# Revit family: Haworth_Epure_Pedestal_Mobile_EU_PRELIMINARY
name_source: partatom
category: Furniture
units: mm (PartAtom-declared; Revit-internal decimal feet)

## family parameters
Always vertical = Yes
Cut with Voids When Loaded = No
OmniClass Number = 23.40.70.14.64.11
OmniClass Title = Office Furniture
Room Calculation Point = No
Shared = No
Work Plane-Based = No

## types (5) — shared parameters
Actual Depth = 59 cm
Actual Height = 58 cm
Actual Width = 44 cm
Assembly Code = E2020200
Description = Haworth - Epure - Mobile Pedestal
Filing Drawer Large = 17 cm
Filing Drawer Medium = 16 cm
Filing Drawer Small = 15 cm
Glide Finish = Haworth _ Polymer _ Black
Manufacturer = Haworth
Model = EUMP59FXXX
Pen Drawer = 5 cm
Revision Number = 1
Simple Drawer = 32 cm
Size = Verify Final Dim.w/ Haworth
URL = https://www.haworth.com
URL - Product = https://www.haworth.com
Warranty = http://www.haworth.com

## per-type parameters (varying)
| type | Filing Drawer = 13cm | Filing Drawer = 16cm | Filing Drawer = 19cm | Filing Drawers = 16cm 3 Drawers | Handle 1 | Handle 2 | Metal Handle | Pen Drawer = 5cm | Simple Drawer = 32cm | Trim Finish | with Pull | without Pull |
| 2 Drawers without Pen Tray | No | Yes | No | No | No | Yes | No | No | Yes | Haworth _ Paint _ Smooth Plaster | Yes | No |
| 2 Drawers with Pen Tray | No | Yes | No | No | Yes | No | No | No | Yes | Haworth _ Polymer _ Undecided | Yes | No |
| 3 Drawers without Pen Tray | No | Yes | Yes | Yes | No | No | No | No | No | Haworth _ Polymer _ Undecided | No | Yes |
| 3 Drawers with Pen Tray | Yes | No | Yes | Yes | No | No | Yes | Yes | No | Haworth _ Paint _ Smooth Plaster | Yes | No |
| 2 Drawers with Pen Drawer | No | Yes | No | No | No | No | No | Yes | Yes | Haworth _ Polymer _ Undecided | No | Yes |

## geometry (parser evidence)
native form markers: Sweep x4
no freeform markers — native parametric forms only
